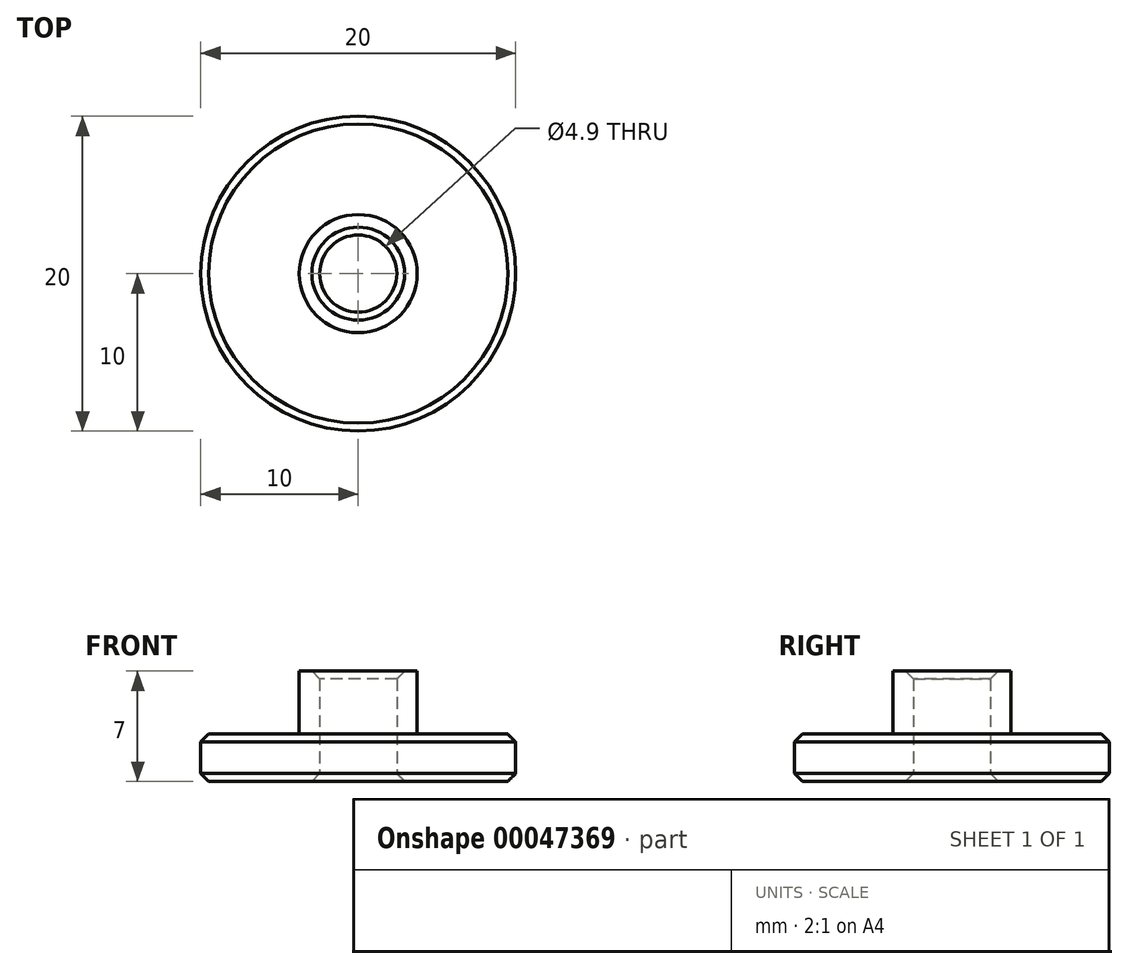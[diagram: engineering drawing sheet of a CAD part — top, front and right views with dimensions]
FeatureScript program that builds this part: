
annotation { "Feature Type Name" : "Feature", "Feature Type Description" : "" }
export const myFeature = defineFeature(function(context is Context, id is Id, definition is map)
    precondition{}
    {
        {
            var Q0;
            Q0=qCreatedBy(makeId("Top.planeOp"),FACE);
            var sketch = newSketch(context, id + "F0", { "sketchPlane" : qUnion([Q0])});
            skCircle(sketch, "E0", {"center": v(0, 0) * mm, "radius": 2.45 * mm});
            skCircle(sketch, "E1", {"center": v(0, 0) * mm, "radius": 10 * mm});
            skSolve(sketch);
        }
        {
            var Q0;
            Q0 = qSketchRegion(id + "F0", true);
            extrude(context, id + "F1", {"entities" : qUnion([Q0]), "depth" : 3 * mm, "offsetDistance" : 25 * mm});
        }
        {
            var Q0;
            Q0=makeQuery(id+"F1.opExtrude","CAP_FACE",FACE,{"disambiguationData":[OSD([sQuery(id+"F0.wireOp",EDGE,"E0"),sQuery(id+"F0.wireOp",EDGE,"E1")])],"isStart":false});
            var sketch = newSketch(context, id + "F2", { "sketchPlane" : qUnion([Q0])});
            skCircle(sketch, "E2", {"center": v(0, 0) * mm, "radius": 3.75 * mm});
            skSolve(sketch);
        }
        {
            var Q0;
            Q0=makeQuery(id+"F2.imprint","IMPRINT",FACE,{"disambiguationData":[TD([[makeQuery(id+"F2.imprint","IMPRINT",EDGE,{"derivedFrom":sQuery(id+"F2.wireOp",EDGE,"E2")}),1.0]])]});
            extrude(context, id + "F3", {"entities" : qUnion([Q0]), "operationType" : NewBodyOperationType.ADD, "depth" : 4 * mm, "offsetDistance" : 25 * mm});
        }
        {
            var Q0;
            Q0=makeQuery(id+"F1.opExtrude","CAP_EDGE",EDGE,{"disambiguationData":[OSD([sQuery(id+"F0.wireOp",EDGE,"E1")])],"isStart":false});
            var Q1;
            Q1=makeQuery(id+"F3.opExtrude","CAP_EDGE",EDGE,{"disambiguationData":[OSD([sQuery(id+"F0.wireOp",EDGE,"E0")])],"isStart":false});
            var Q2;
            Q2=makeQuery(id+"F1.opExtrude","CAP_FACE",FACE,{"disambiguationData":[OSD([sQuery(id+"F0.wireOp",EDGE,"E0"),sQuery(id+"F0.wireOp",EDGE,"E1")])],"isStart":true});
            chamfer(context, id + "F4", {"entities" : qUnion([Q0, Q1, Q2]), "width" : .5 * mm, "tangentPropagation" : true});
        }
    });
